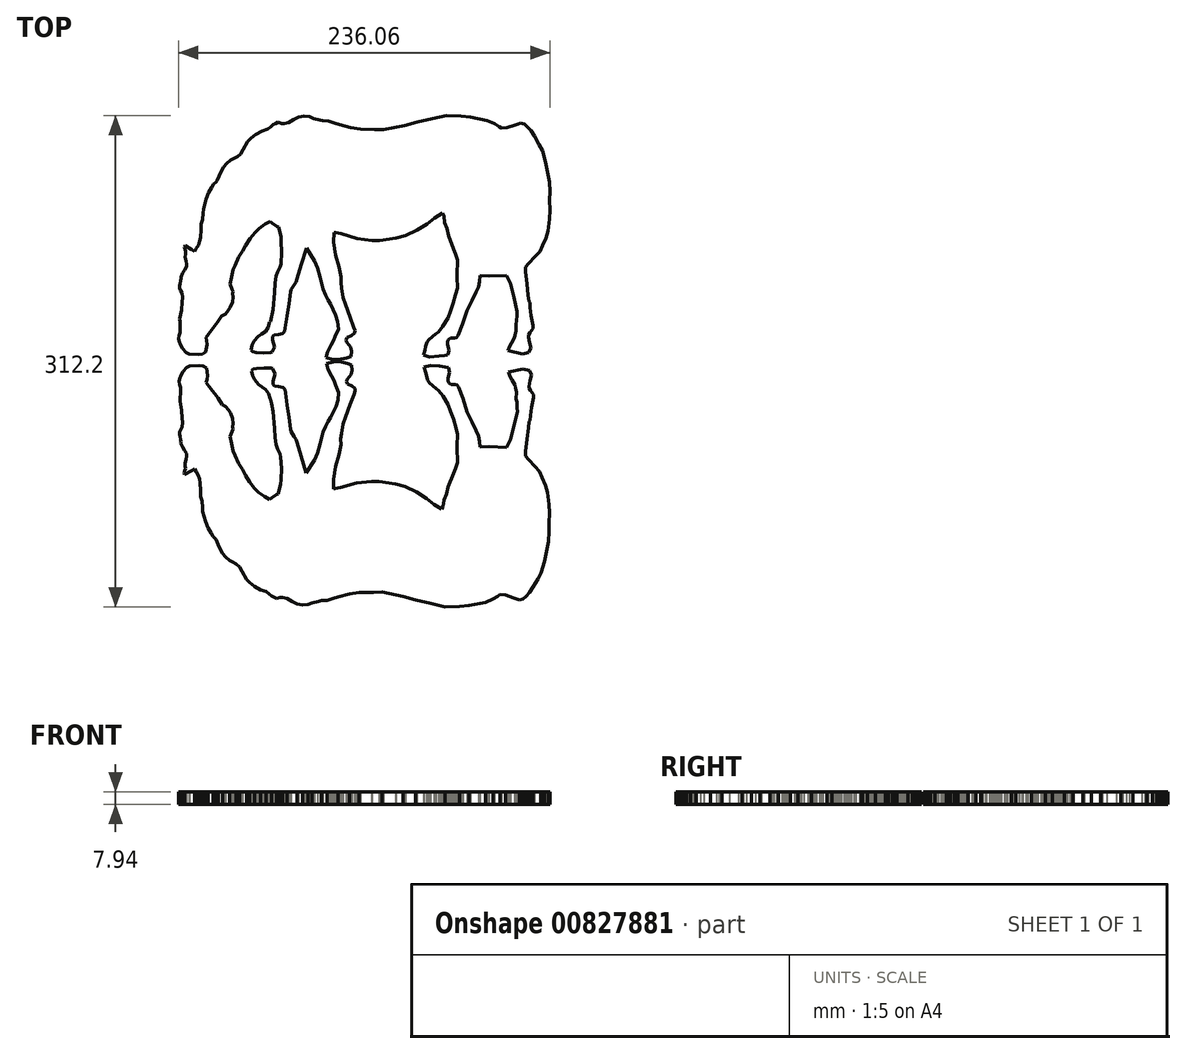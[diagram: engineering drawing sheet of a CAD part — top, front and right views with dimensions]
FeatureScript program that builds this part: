
annotation { "Feature Type Name" : "Feature", "Feature Type Description" : "" }
export const myFeature = defineFeature(function(context is Context, id is Id, definition is map)
    precondition{}
    {
        {
            var Q0;
            Q0=qCreatedBy(makeId("Top.planeOp"),FACE);
            var sketch = newSketch(context, id + "F0", { "sketchPlane" : qUnion([Q0])});
            skLineSegment(sketch, "E0", {"start": v(-100.7, 5.73) * mm, "end": v(-102.84, 4.52) * mm});
            skLineSegment(sketch, "E1", {"start": v(-102.84, 4.52) * mm, "end": v(-105.3, 4.23) * mm});
            skLineSegment(sketch, "E2", {"start": v(-105.3, 4.23) * mm, "end": v(-111.22, 4.55) * mm});
            skLineSegment(sketch, "E3", {"start": v(-111.22, 4.55) * mm, "end": v(-113.36, 5.41) * mm});
            skLineSegment(sketch, "E4", {"start": v(-113.36, 5.41) * mm, "end": v(-115.5, 7.9) * mm});
            skLineSegment(sketch, "E5", {"start": v(-115.5, 7.9) * mm, "end": v(-116.75, 10.19) * mm});
            skLineSegment(sketch, "E6", {"start": v(-116.75, 10.19) * mm, "end": v(-117.54, 12.83) * mm});
            skLineSegment(sketch, "E7", {"start": v(-117.54, 12.83) * mm, "end": v(-118.03, 14.5) * mm});
            skLineSegment(sketch, "E8", {"start": v(-118.03, 14.5) * mm, "end": v(-117.54, 16.28) * mm});
            skLineSegment(sketch, "E9", {"start": v(-117.54, 16.28) * mm, "end": v(-116.98, 18.27) * mm});
            skLineSegment(sketch, "E10", {"start": v(-116.98, 18.27) * mm, "end": v(-117.07, 21.4) * mm});
            skLineSegment(sketch, "E11", {"start": v(-117.07, 21.4) * mm, "end": v(-117.18, 25.1) * mm});
            skLineSegment(sketch, "E12", {"start": v(-117.18, 25.1) * mm, "end": v(-117.22, 26.75) * mm});
            skLineSegment(sketch, "E13", {"start": v(-117.22, 26.75) * mm, "end": v(-116.18, 32.64) * mm});
            skLineSegment(sketch, "E14", {"start": v(-116.18, 32.64) * mm, "end": v(-115.72, 37.46) * mm});
            skLineSegment(sketch, "E15", {"start": v(-115.72, 37.46) * mm, "end": v(-115.44, 40.37) * mm});
            skLineSegment(sketch, "E16", {"start": v(-115.44, 40.37) * mm, "end": v(-115.83, 43.17) * mm});
            skLineSegment(sketch, "E17", {"start": v(-115.83, 43.17) * mm, "end": v(-116.65, 45.02) * mm});
            skLineSegment(sketch, "E18", {"start": v(-116.65, 45.02) * mm, "end": v(-117.3, 46.51) * mm});
            skLineSegment(sketch, "E19", {"start": v(-117.3, 46.51) * mm, "end": v(-117.47, 47.93) * mm});
            skLineSegment(sketch, "E20", {"start": v(-117.47, 47.93) * mm, "end": v(-117.04, 49) * mm});
            skLineSegment(sketch, "E21", {"start": v(-117.04, 49) * mm, "end": v(-116.58, 51.39) * mm});
            skLineSegment(sketch, "E22", {"start": v(-116.58, 51.39) * mm, "end": v(-116.37, 52.44) * mm});
            skLineSegment(sketch, "E23", {"start": v(-116.37, 52.44) * mm, "end": v(-116.54, 53.31) * mm});
            skLineSegment(sketch, "E24", {"start": v(-116.54, 53.31) * mm, "end": v(-115.47, 55.98) * mm});
            skLineSegment(sketch, "E25", {"start": v(-115.47, 55.98) * mm, "end": v(-114.18, 58.03) * mm});
            skLineSegment(sketch, "E26", {"start": v(-114.18, 58.03) * mm, "end": v(-112.93, 60.03) * mm});
            skLineSegment(sketch, "E27", {"start": v(-112.93, 60.03) * mm, "end": v(-112.76, 61.56) * mm});
            skLineSegment(sketch, "E28", {"start": v(-112.76, 61.56) * mm, "end": v(-113.22, 63.77) * mm});
            skLineSegment(sketch, "E29", {"start": v(-113.22, 63.77) * mm, "end": v(-113.73, 66.2) * mm});
            skLineSegment(sketch, "E30", {"start": v(-113.73, 66.2) * mm, "end": v(-113.61, 68.08) * mm});
            skLineSegment(sketch, "E31", {"start": v(-113.61, 68.08) * mm, "end": v(-113.52, 69.6) * mm});
            skLineSegment(sketch, "E32", {"start": v(-113.52, 69.6) * mm, "end": v(-114, 71.1) * mm});
            skLineSegment(sketch, "E33", {"start": v(-114, 71.1) * mm, "end": v(-114.42, 72.38) * mm});
            skLineSegment(sketch, "E34", {"start": v(-114.42, 72.38) * mm, "end": v(-113.93, 73.53) * mm});
            skLineSegment(sketch, "E35", {"start": v(-113.93, 73.53) * mm, "end": v(-109.87, 71.07) * mm});
            skLineSegment(sketch, "E36", {"start": v(-109.87, 71.07) * mm, "end": v(-107.76, 69.8) * mm});
            skLineSegment(sketch, "E37", {"start": v(-107.76, 69.8) * mm, "end": v(-106.77, 71.46) * mm});
            skLineSegment(sketch, "E38", {"start": v(-106.77, 71.46) * mm, "end": v(-105.38, 73.76) * mm});
            skLineSegment(sketch, "E39", {"start": v(-105.38, 73.76) * mm, "end": v(-104.48, 76.16) * mm});
            skLineSegment(sketch, "E40", {"start": v(-104.48, 76.16) * mm, "end": v(-104.05, 78.66) * mm});
            skLineSegment(sketch, "E41", {"start": v(-104.05, 78.66) * mm, "end": v(-103.77, 83.58) * mm});
            skLineSegment(sketch, "E42", {"start": v(-103.77, 83.58) * mm, "end": v(-103.56, 87.1) * mm});
            skLineSegment(sketch, "E43", {"start": v(-103.56, 87.1) * mm, "end": v(-102.6, 90.12) * mm});
            skLineSegment(sketch, "E44", {"start": v(-102.6, 90.12) * mm, "end": v(-102.38, 94.22) * mm});
            skLineSegment(sketch, "E45", {"start": v(-102.38, 94.22) * mm, "end": v(-102.25, 96.66) * mm});
            skLineSegment(sketch, "E46", {"start": v(-102.25, 96.66) * mm, "end": v(-100.48, 103.12) * mm});
            skLineSegment(sketch, "E47", {"start": v(-100.48, 103.12) * mm, "end": v(-98.84, 107.15) * mm});
            skLineSegment(sketch, "E48", {"start": v(-98.84, 107.15) * mm, "end": v(-96.95, 110.4) * mm});
            skLineSegment(sketch, "E49", {"start": v(-96.95, 110.4) * mm, "end": v(-95.64, 112.65) * mm});
            skLineSegment(sketch, "E50", {"start": v(-95.64, 112.65) * mm, "end": v(-94.24, 113.92) * mm});
            skLineSegment(sketch, "E51", {"start": v(-94.24, 113.92) * mm, "end": v(-93.52, 114.58) * mm});
            skLineSegment(sketch, "E52", {"start": v(-93.52, 114.58) * mm, "end": v(-92.42, 117.61) * mm});
            skLineSegment(sketch, "E53", {"start": v(-92.42, 117.61) * mm, "end": v(-90.74, 121.03) * mm});
            skLineSegment(sketch, "E54", {"start": v(-90.74, 121.03) * mm, "end": v(-89.56, 123.44) * mm});
            skLineSegment(sketch, "E55", {"start": v(-89.56, 123.44) * mm, "end": v(-87.46, 125.38) * mm});
            skLineSegment(sketch, "E56", {"start": v(-87.46, 125.38) * mm, "end": v(-84.9, 127.75) * mm});
            skLineSegment(sketch, "E57", {"start": v(-84.9, 127.75) * mm, "end": v(-83.1, 128.71) * mm});
            skLineSegment(sketch, "E58", {"start": v(-83.1, 128.71) * mm, "end": v(-80.64, 130.04) * mm});
            skLineSegment(sketch, "E59", {"start": v(-80.64, 130.04) * mm, "end": v(-78.58, 131.7) * mm});
            skLineSegment(sketch, "E60", {"start": v(-78.58, 131.7) * mm, "end": v(-76.97, 134.56) * mm});
            skLineSegment(sketch, "E61", {"start": v(-76.97, 134.56) * mm, "end": v(-74.14, 139.6) * mm});
            skLineSegment(sketch, "E62", {"start": v(-74.14, 139.6) * mm, "end": v(-72.08, 141.6) * mm});
            skLineSegment(sketch, "E63", {"start": v(-72.08, 141.6) * mm, "end": v(-69.04, 143.96) * mm});
            skLineSegment(sketch, "E64", {"start": v(-69.04, 143.96) * mm, "end": v(-64.94, 146.24) * mm});
            skLineSegment(sketch, "E65", {"start": v(-64.94, 146.24) * mm, "end": v(-61.4, 147.28) * mm});
            skLineSegment(sketch, "E66", {"start": v(-61.4, 147.28) * mm, "end": v(-59.7, 148.7) * mm});
            skLineSegment(sketch, "E67", {"start": v(-59.7, 148.7) * mm, "end": v(-57.97, 150.14) * mm});
            skLineSegment(sketch, "E68", {"start": v(-57.97, 150.14) * mm, "end": v(-56.3, 150.99) * mm});
            skLineSegment(sketch, "E69", {"start": v(-56.3, 150.99) * mm, "end": v(-54.8, 151.75) * mm});
            skLineSegment(sketch, "E70", {"start": v(-54.8, 151.75) * mm, "end": v(-52.55, 151.06) * mm});
            skLineSegment(sketch, "E71", {"start": v(-52.55, 151.06) * mm, "end": v(-50.97, 151.06) * mm});
            skLineSegment(sketch, "E72", {"start": v(-50.97, 151.06) * mm, "end": v(-48.08, 151.7) * mm});
            skLineSegment(sketch, "E73", {"start": v(-48.08, 151.7) * mm, "end": v(-44.9, 153.38) * mm});
            skLineSegment(sketch, "E74", {"start": v(-44.9, 153.38) * mm, "end": v(-41.94, 154.95) * mm});
            skLineSegment(sketch, "E75", {"start": v(-41.94, 154.95) * mm, "end": v(-38.23, 155.6) * mm});
            skLineSegment(sketch, "E76", {"start": v(-38.23, 155.6) * mm, "end": v(-34.95, 155.24) * mm});
            skLineSegment(sketch, "E77", {"start": v(-34.95, 155.24) * mm, "end": v(-32.17, 154.17) * mm});
            skLineSegment(sketch, "E78", {"start": v(-32.17, 154.17) * mm, "end": v(-28.2, 153.2) * mm});
            skLineSegment(sketch, "E79", {"start": v(-28.2, 153.2) * mm, "end": v(-26.4, 152.77) * mm});
            skLineSegment(sketch, "E80", {"start": v(-26.4, 152.77) * mm, "end": v(-22.67, 152.56) * mm});
            skLineSegment(sketch, "E81", {"start": v(-22.67, 152.56) * mm, "end": v(-19, 151.31) * mm});
            skLineSegment(sketch, "E82", {"start": v(-19, 151.31) * mm, "end": v(-15.75, 150.21) * mm});
            skLineSegment(sketch, "E83", {"start": v(-15.75, 150.21) * mm, "end": v(-8.64, 148.28) * mm});
            skLineSegment(sketch, "E84", {"start": v(-8.64, 148.28) * mm, "end": v(-2.42, 147.5) * mm});
            skLineSegment(sketch, "E85", {"start": v(-2.42, 147.5) * mm, "end": v(6.6, 147.18) * mm});
            skLineSegment(sketch, "E86", {"start": v(6.6, 147.18) * mm, "end": v(12.16, 146.98) * mm});
            skLineSegment(sketch, "E87", {"start": v(12.16, 146.98) * mm, "end": v(25.56, 149.6) * mm});
            skLineSegment(sketch, "E88", {"start": v(25.56, 149.6) * mm, "end": v(33.52, 151.92) * mm});
            skLineSegment(sketch, "E89", {"start": v(33.52, 151.92) * mm, "end": v(43.16, 154.07) * mm});
            skLineSegment(sketch, "E90", {"start": v(43.16, 154.07) * mm, "end": v(52.32, 156.1) * mm});
            skLineSegment(sketch, "E91", {"start": v(52.32, 156.1) * mm, "end": v(61.44, 155.75) * mm});
            skLineSegment(sketch, "E92", {"start": v(61.44, 155.75) * mm, "end": v(67.36, 155.03) * mm});
            skLineSegment(sketch, "E93", {"start": v(67.36, 155.03) * mm, "end": v(77.8, 152.96) * mm});
            skLineSegment(sketch, "E94", {"start": v(77.8, 152.96) * mm, "end": v(82.55, 150.82) * mm});
            skLineSegment(sketch, "E95", {"start": v(82.55, 150.82) * mm, "end": v(85.4, 149.04) * mm});
            skLineSegment(sketch, "E96", {"start": v(85.4, 149.04) * mm, "end": v(87.15, 147.95) * mm});
            skLineSegment(sketch, "E97", {"start": v(87.15, 147.95) * mm, "end": v(90.5, 148.25) * mm});
            skLineSegment(sketch, "E98", {"start": v(90.5, 148.25) * mm, "end": v(95.74, 149.97) * mm});
            skLineSegment(sketch, "E99", {"start": v(95.74, 149.97) * mm, "end": v(97.57, 150.56) * mm});
            skLineSegment(sketch, "E100", {"start": v(97.57, 150.56) * mm, "end": v(99.3, 151.12) * mm});
            skLineSegment(sketch, "E101", {"start": v(99.3, 151.12) * mm, "end": v(101.57, 150.54) * mm});
            skLineSegment(sketch, "E102", {"start": v(101.57, 150.54) * mm, "end": v(103.39, 149.11) * mm});
            skLineSegment(sketch, "E103", {"start": v(103.39, 149.11) * mm, "end": v(105.74, 146.44) * mm});
            skLineSegment(sketch, "E104", {"start": v(105.74, 146.44) * mm, "end": v(108.04, 143.04) * mm});
            skLineSegment(sketch, "E105", {"start": v(108.04, 143.04) * mm, "end": v(110.96, 137.65) * mm});
            skLineSegment(sketch, "E106", {"start": v(110.96, 137.65) * mm, "end": v(113.04, 133.84) * mm});
            skLineSegment(sketch, "E107", {"start": v(113.04, 133.84) * mm, "end": v(115.07, 126.52) * mm});
            skLineSegment(sketch, "E108", {"start": v(115.07, 126.52) * mm, "end": v(116.96, 116.99) * mm});
            skLineSegment(sketch, "E109", {"start": v(116.96, 116.99) * mm, "end": v(117.6, 113.8) * mm});
            skLineSegment(sketch, "E110", {"start": v(117.6, 113.8) * mm, "end": v(117.92, 107.7) * mm});
            skLineSegment(sketch, "E111", {"start": v(117.92, 107.7) * mm, "end": v(117.74, 102.32) * mm});
            skLineSegment(sketch, "E112", {"start": v(117.74, 102.32) * mm, "end": v(118.03, 95.84) * mm});
            skLineSegment(sketch, "E113", {"start": v(118.03, 95.84) * mm, "end": v(117.57, 90.43) * mm});
            skLineSegment(sketch, "E114", {"start": v(117.57, 90.43) * mm, "end": v(116.62, 82.82) * mm});
            skLineSegment(sketch, "E115", {"start": v(116.62, 82.82) * mm, "end": v(115.27, 78.29) * mm});
            skLineSegment(sketch, "E116", {"start": v(115.27, 78.29) * mm, "end": v(113.11, 73.3) * mm});
            skLineSegment(sketch, "E117", {"start": v(113.11, 73.3) * mm, "end": v(111.47, 69.5) * mm});
            skLineSegment(sketch, "E118", {"start": v(111.47, 69.5) * mm, "end": v(108.52, 66.36) * mm});
            skLineSegment(sketch, "E119", {"start": v(108.52, 66.36) * mm, "end": v(104.39, 61.97) * mm});
            skLineSegment(sketch, "E120", {"start": v(104.39, 61.97) * mm, "end": v(102.38, 59.83) * mm});
            skLineSegment(sketch, "E121", {"start": v(102.38, 59.83) * mm, "end": v(102.47, 56.84) * mm});
            skLineSegment(sketch, "E122", {"start": v(102.47, 56.84) * mm, "end": v(103.32, 49.1) * mm});
            skLineSegment(sketch, "E123", {"start": v(103.32, 49.1) * mm, "end": v(104.1, 41.96) * mm});
            skLineSegment(sketch, "E124", {"start": v(104.1, 41.96) * mm, "end": v(104.55, 37.87) * mm});
            skLineSegment(sketch, "E125", {"start": v(104.55, 37.87) * mm, "end": v(105.16, 37.35) * mm});
            skLineSegment(sketch, "E126", {"start": v(105.16, 37.35) * mm, "end": v(105.3, 34.17) * mm});
            skLineSegment(sketch, "E127", {"start": v(105.3, 34.17) * mm, "end": v(105.94, 29.06) * mm});
            skLineSegment(sketch, "E128", {"start": v(105.94, 29.06) * mm, "end": v(107.21, 22.74) * mm});
            skLineSegment(sketch, "E129", {"start": v(107.21, 22.74) * mm, "end": v(107.18, 20.76) * mm});
            skLineSegment(sketch, "E130", {"start": v(107.18, 20.76) * mm, "end": v(105.12, 18.24) * mm});
            skLineSegment(sketch, "E131", {"start": v(105.12, 18.24) * mm, "end": v(104.31, 16.61) * mm});
            skLineSegment(sketch, "E132", {"start": v(104.31, 16.61) * mm, "end": v(104.16, 15.47) * mm});
            skLineSegment(sketch, "E133", {"start": v(104.16, 15.47) * mm, "end": v(105.05, 11.8) * mm});
            skLineSegment(sketch, "E134", {"start": v(105.05, 11.8) * mm, "end": v(105.9, 8.25) * mm});
            skLineSegment(sketch, "E135", {"start": v(105.9, 8.25) * mm, "end": v(104.41, 5.47) * mm});
            skLineSegment(sketch, "E136", {"start": v(104.41, 5.47) * mm, "end": v(100.31, 4.62) * mm});
            skLineSegment(sketch, "E137", {"start": v(100.31, 4.62) * mm, "end": v(91.37, 6.67) * mm});
            skLineSegment(sketch, "E138", {"start": v(91.37, 6.67) * mm, "end": v(92.22, 9.32) * mm});
            skLineSegment(sketch, "E139", {"start": v(92.22, 9.32) * mm, "end": v(93.42, 11.44) * mm});
            skLineSegment(sketch, "E140", {"start": v(93.42, 11.44) * mm, "end": v(95.37, 14.89) * mm});
            skLineSegment(sketch, "E141", {"start": v(95.37, 14.89) * mm, "end": v(95.75, 16.5) * mm});
            skLineSegment(sketch, "E142", {"start": v(95.75, 16.5) * mm, "end": v(96.39, 19.19) * mm});
            skLineSegment(sketch, "E143", {"start": v(96.39, 19.19) * mm, "end": v(96.21, 23.65) * mm});
            skLineSegment(sketch, "E144", {"start": v(96.21, 23.65) * mm, "end": v(96.74, 25.59) * mm});
            skLineSegment(sketch, "E145", {"start": v(96.74, 25.59) * mm, "end": v(96.92, 29.2) * mm});
            skLineSegment(sketch, "E146", {"start": v(96.92, 29.2) * mm, "end": v(97.04, 31.61) * mm});
            skLineSegment(sketch, "E147", {"start": v(97.04, 31.61) * mm, "end": v(94.94, 40.44) * mm});
            skLineSegment(sketch, "E148", {"start": v(94.94, 40.44) * mm, "end": v(92.83, 49.31) * mm});
            skLineSegment(sketch, "E149", {"start": v(92.83, 49.31) * mm, "end": v(90.27, 54.43) * mm});
            skLineSegment(sketch, "E150", {"start": v(90.27, 54.43) * mm, "end": v(79.12, 54.07) * mm});
            skLineSegment(sketch, "E151", {"start": v(79.12, 54.07) * mm, "end": v(73.57, 54.32) * mm});
            skLineSegment(sketch, "E152", {"start": v(73.57, 54.32) * mm, "end": v(73.11, 50.75) * mm});
            skLineSegment(sketch, "E153", {"start": v(73.11, 50.75) * mm, "end": v(72.66, 47.22) * mm});
            skLineSegment(sketch, "E154", {"start": v(72.66, 47.22) * mm, "end": v(70.99, 43.89) * mm});
            skLineSegment(sketch, "E155", {"start": v(70.99, 43.89) * mm, "end": v(68.3, 38.52) * mm});
            skLineSegment(sketch, "E156", {"start": v(68.3, 38.52) * mm, "end": v(65.06, 32.05) * mm});
            skLineSegment(sketch, "E157", {"start": v(65.06, 32.05) * mm, "end": v(62.46, 23.55) * mm});
            skLineSegment(sketch, "E158", {"start": v(62.46, 23.55) * mm, "end": v(59.6, 16.19) * mm});
            skLineSegment(sketch, "E159", {"start": v(59.6, 16.19) * mm, "end": v(58.43, 15.02) * mm});
            skLineSegment(sketch, "E160", {"start": v(58.43, 15.02) * mm, "end": v(57.36, 14.7) * mm});
            skLineSegment(sketch, "E161", {"start": v(57.36, 14.7) * mm, "end": v(54.85, 14.62) * mm});
            skLineSegment(sketch, "E162", {"start": v(54.85, 14.62) * mm, "end": v(53.44, 13.7) * mm});
            skLineSegment(sketch, "E163", {"start": v(53.44, 13.7) * mm, "end": v(52.73, 12.6) * mm});
            skLineSegment(sketch, "E164", {"start": v(52.73, 12.6) * mm, "end": v(52.88, 10.56) * mm});
            skLineSegment(sketch, "E165", {"start": v(52.88, 10.56) * mm, "end": v(53.9, 7.03) * mm});
            skLineSegment(sketch, "E166", {"start": v(53.9, 7.03) * mm, "end": v(53.48, 5.65) * mm});
            skLineSegment(sketch, "E167", {"start": v(53.48, 5.65) * mm, "end": v(52.94, 3.9) * mm});
            skLineSegment(sketch, "E168", {"start": v(52.94, 3.9) * mm, "end": v(50.88, 3.62) * mm});
            skLineSegment(sketch, "E169", {"start": v(50.88, 3.62) * mm, "end": v(47.5, 3.16) * mm});
            skLineSegment(sketch, "E170", {"start": v(47.5, 3.16) * mm, "end": v(41.55, 2.8) * mm});
            skLineSegment(sketch, "E171", {"start": v(41.55, 2.8) * mm, "end": v(37.66, 3.83) * mm});
            skLineSegment(sketch, "E172", {"start": v(37.66, 3.83) * mm, "end": v(38.44, 6.97) * mm});
            skLineSegment(sketch, "E173", {"start": v(38.44, 6.97) * mm, "end": v(39.02, 9.32) * mm});
            skLineSegment(sketch, "E174", {"start": v(39.02, 9.32) * mm, "end": v(39.7, 12.1) * mm});
            skLineSegment(sketch, "E175", {"start": v(39.7, 12.1) * mm, "end": v(41.21, 13.92) * mm});
            skLineSegment(sketch, "E176", {"start": v(41.21, 13.92) * mm, "end": v(45.14, 17.42) * mm});
            skLineSegment(sketch, "E177", {"start": v(45.14, 17.42) * mm, "end": v(47.01, 18.55) * mm});
            skLineSegment(sketch, "E178", {"start": v(47.01, 18.55) * mm, "end": v(49.7, 22.04) * mm});
            skLineSegment(sketch, "E179", {"start": v(49.7, 22.04) * mm, "end": v(53, 27.39) * mm});
            skLineSegment(sketch, "E180", {"start": v(53, 27.39) * mm, "end": v(54.73, 32.02) * mm});
            skLineSegment(sketch, "E181", {"start": v(54.73, 32.02) * mm, "end": v(56.45, 36.61) * mm});
            skLineSegment(sketch, "E182", {"start": v(56.45, 36.61) * mm, "end": v(58.05, 42.43) * mm});
            skLineSegment(sketch, "E183", {"start": v(58.05, 42.43) * mm, "end": v(59.2, 46.55) * mm});
            skLineSegment(sketch, "E184", {"start": v(59.2, 46.55) * mm, "end": v(58.8, 53.5) * mm});
            skLineSegment(sketch, "E185", {"start": v(58.8, 53.5) * mm, "end": v(59.01, 57.89) * mm});
            skLineSegment(sketch, "E186", {"start": v(59.01, 57.89) * mm, "end": v(59.17, 61.19) * mm});
            skLineSegment(sketch, "E187", {"start": v(59.17, 61.19) * mm, "end": v(59.32, 64.21) * mm});
            skLineSegment(sketch, "E188", {"start": v(59.32, 64.21) * mm, "end": v(57.95, 67.97) * mm});
            skLineSegment(sketch, "E189", {"start": v(57.95, 67.97) * mm, "end": v(56.76, 71.24) * mm});
            skLineSegment(sketch, "E190", {"start": v(56.76, 71.24) * mm, "end": v(53.52, 79.78) * mm});
            skLineSegment(sketch, "E191", {"start": v(53.52, 79.78) * mm, "end": v(52.4, 84.29) * mm});
            skLineSegment(sketch, "E192", {"start": v(52.4, 84.29) * mm, "end": v(50.9, 88.06) * mm});
            skLineSegment(sketch, "E193", {"start": v(50.9, 88.06) * mm, "end": v(50.5, 92.27) * mm});
            skLineSegment(sketch, "E194", {"start": v(50.5, 92.27) * mm, "end": v(49.52, 93.95) * mm});
            skLineSegment(sketch, "E195", {"start": v(49.52, 93.95) * mm, "end": v(44.7, 91.07) * mm});
            skLineSegment(sketch, "E196", {"start": v(44.7, 91.07) * mm, "end": v(39.75, 87.18) * mm});
            skLineSegment(sketch, "E197", {"start": v(39.75, 87.18) * mm, "end": v(33.54, 83.37) * mm});
            skLineSegment(sketch, "E198", {"start": v(33.54, 83.37) * mm, "end": v(26.01, 79.84) * mm});
            skLineSegment(sketch, "E199", {"start": v(26.01, 79.84) * mm, "end": v(20.1, 78.2) * mm});
            skLineSegment(sketch, "E200", {"start": v(20.1, 78.2) * mm, "end": v(9.61, 76.74) * mm});
            skLineSegment(sketch, "E201", {"start": v(9.61, 76.74) * mm, "end": v(4.97, 76.77) * mm});
            skLineSegment(sketch, "E202", {"start": v(4.97, 76.77) * mm, "end": v(-4.73, 77.97) * mm});
            skLineSegment(sketch, "E203", {"start": v(-4.73, 77.97) * mm, "end": v(-14.7, 80.93) * mm});
            skLineSegment(sketch, "E204", {"start": v(-14.7, 80.93) * mm, "end": v(-18.43, 81.56) * mm});
            skLineSegment(sketch, "E205", {"start": v(-18.43, 81.56) * mm, "end": v(-19.37, 81.72) * mm});
            skLineSegment(sketch, "E206", {"start": v(-19.37, 81.72) * mm, "end": v(-19.44, 75.66) * mm});
            skLineSegment(sketch, "E207", {"start": v(-19.44, 75.66) * mm, "end": v(-18.17, 67.45) * mm});
            skLineSegment(sketch, "E208", {"start": v(-18.17, 67.45) * mm, "end": v(-15.96, 59.93) * mm});
            skLineSegment(sketch, "E209", {"start": v(-15.96, 59.93) * mm, "end": v(-15.14, 55.01) * mm});
            skLineSegment(sketch, "E210", {"start": v(-15.14, 55.01) * mm, "end": v(-14.88, 53.5) * mm});
            skLineSegment(sketch, "E211", {"start": v(-14.88, 53.5) * mm, "end": v(-14.95, 50.03) * mm});
            skLineSegment(sketch, "E212", {"start": v(-14.95, 50.03) * mm, "end": v(-14.61, 46.44) * mm});
            skLineSegment(sketch, "E213", {"start": v(-14.61, 46.44) * mm, "end": v(-13.5, 40.34) * mm});
            skLineSegment(sketch, "E214", {"start": v(-13.5, 40.34) * mm, "end": v(-11.96, 36.08) * mm});
            skLineSegment(sketch, "E215", {"start": v(-11.96, 36.08) * mm, "end": v(-9.1, 28.1) * mm});
            skLineSegment(sketch, "E216", {"start": v(-9.1, 28.1) * mm, "end": v(-6.74, 21.56) * mm});
            skLineSegment(sketch, "E217", {"start": v(-6.74, 21.56) * mm, "end": v(-6.01, 19.55) * mm});
            skLineSegment(sketch, "E218", {"start": v(-6.01, 19.55) * mm, "end": v(-6.2, 17.79) * mm});
            skLineSegment(sketch, "E219", {"start": v(-6.2, 17.79) * mm, "end": v(-8.22, 16.37) * mm});
            skLineSegment(sketch, "E220", {"start": v(-8.22, 16.37) * mm, "end": v(-10.9, 14.98) * mm});
            skLineSegment(sketch, "E221", {"start": v(-10.9, 14.98) * mm, "end": v(-11.47, 13.53) * mm});
            skLineSegment(sketch, "E222", {"start": v(-11.47, 13.53) * mm, "end": v(-11.17, 12.03) * mm});
            skLineSegment(sketch, "E223", {"start": v(-11.17, 12.03) * mm, "end": v(-9.86, 10.35) * mm});
            skLineSegment(sketch, "E224", {"start": v(-9.86, 10.35) * mm, "end": v(-8.7, 8.85) * mm});
            skLineSegment(sketch, "E225", {"start": v(-8.7, 8.85) * mm, "end": v(-8.18, 6.38) * mm});
            skLineSegment(sketch, "E226", {"start": v(-8.18, 6.38) * mm, "end": v(-8.44, 2.89) * mm});
            skLineSegment(sketch, "E227", {"start": v(-8.44, 2.89) * mm, "end": v(-11.17, 1.92) * mm});
            skLineSegment(sketch, "E228", {"start": v(-11.17, 1.92) * mm, "end": v(-16.3, 0.94) * mm});
            skLineSegment(sketch, "E229", {"start": v(-16.3, 0.94) * mm, "end": v(-20.12, 1.05) * mm});
            skLineSegment(sketch, "E230", {"start": v(-20.12, 1.05) * mm, "end": v(-24.27, 2.25) * mm});
            skLineSegment(sketch, "E231", {"start": v(-24.27, 2.25) * mm, "end": v(-23.52, 5.99) * mm});
            skLineSegment(sketch, "E232", {"start": v(-23.52, 5.99) * mm, "end": v(-21.2, 10.18) * mm});
            skLineSegment(sketch, "E233", {"start": v(-21.2, 10.18) * mm, "end": v(-19.65, 12.98) * mm});
            skLineSegment(sketch, "E234", {"start": v(-19.65, 12.98) * mm, "end": v(-18.62, 15.82) * mm});
            skLineSegment(sketch, "E235", {"start": v(-18.62, 15.82) * mm, "end": v(-16.49, 20.51) * mm});
            skLineSegment(sketch, "E236", {"start": v(-16.49, 20.51) * mm, "end": v(-16.86, 25.08) * mm});
            skLineSegment(sketch, "E237", {"start": v(-16.86, 25.08) * mm, "end": v(-18.29, 29.23) * mm});
            skLineSegment(sketch, "E238", {"start": v(-18.29, 29.23) * mm, "end": v(-21.5, 36.46) * mm});
            skLineSegment(sketch, "E239", {"start": v(-21.5, 36.46) * mm, "end": v(-23, 38.82) * mm});
            skLineSegment(sketch, "E240", {"start": v(-23, 38.82) * mm, "end": v(-24.58, 42.08) * mm});
            skLineSegment(sketch, "E241", {"start": v(-24.58, 42.08) * mm, "end": v(-26.32, 45.7) * mm});
            skLineSegment(sketch, "E242", {"start": v(-26.32, 45.7) * mm, "end": v(-28.02, 53.4) * mm});
            skLineSegment(sketch, "E243", {"start": v(-28.02, 53.4) * mm, "end": v(-29.74, 59.08) * mm});
            skLineSegment(sketch, "E244", {"start": v(-29.74, 59.08) * mm, "end": v(-31.62, 63.58) * mm});
            skLineSegment(sketch, "E245", {"start": v(-31.62, 63.58) * mm, "end": v(-36.7, 71.73) * mm});
            skLineSegment(sketch, "E246", {"start": v(-36.7, 71.73) * mm, "end": v(-40.05, 61.07) * mm});
            skLineSegment(sketch, "E247", {"start": v(-40.05, 61.07) * mm, "end": v(-42.77, 52.38) * mm});
            skLineSegment(sketch, "E248", {"start": v(-42.77, 52.38) * mm, "end": v(-43.4, 50.4) * mm});
            skLineSegment(sketch, "E249", {"start": v(-43.4, 50.4) * mm, "end": v(-44.58, 48.5) * mm});
            skLineSegment(sketch, "E250", {"start": v(-44.58, 48.5) * mm, "end": v(-46.43, 45.54) * mm});
            skLineSegment(sketch, "E251", {"start": v(-46.43, 45.54) * mm, "end": v(-46.82, 43.85) * mm});
            skLineSegment(sketch, "E252", {"start": v(-46.82, 43.85) * mm, "end": v(-47.94, 36.52) * mm});
            skLineSegment(sketch, "E253", {"start": v(-47.94, 36.52) * mm, "end": v(-49.14, 28.74) * mm});
            skLineSegment(sketch, "E254", {"start": v(-49.14, 28.74) * mm, "end": v(-50.32, 21) * mm});
            skLineSegment(sketch, "E255", {"start": v(-50.32, 21) * mm, "end": v(-50.64, 18.9) * mm});
            skLineSegment(sketch, "E256", {"start": v(-50.64, 18.9) * mm, "end": v(-51.8, 17.61) * mm});
            skLineSegment(sketch, "E257", {"start": v(-51.8, 17.61) * mm, "end": v(-54.64, 16.86) * mm});
            skLineSegment(sketch, "E258", {"start": v(-54.64, 16.86) * mm, "end": v(-57.23, 16.6) * mm});
            skLineSegment(sketch, "E259", {"start": v(-57.23, 16.6) * mm, "end": v(-58.2, 15.74) * mm});
            skLineSegment(sketch, "E260", {"start": v(-58.2, 15.74) * mm, "end": v(-58.36, 13.53) * mm});
            skLineSegment(sketch, "E261", {"start": v(-58.36, 13.53) * mm, "end": v(-56.93, 8.96) * mm});
            skLineSegment(sketch, "E262", {"start": v(-56.93, 8.96) * mm, "end": v(-58.66, 5.7) * mm});
            skLineSegment(sketch, "E263", {"start": v(-58.66, 5.7) * mm, "end": v(-59.48, 5.4) * mm});
            skLineSegment(sketch, "E264", {"start": v(-59.48, 5.4) * mm, "end": v(-64.1, 5.25) * mm});
            skLineSegment(sketch, "E265", {"start": v(-64.1, 5.25) * mm, "end": v(-68.93, 5.55) * mm});
            skLineSegment(sketch, "E266", {"start": v(-68.93, 5.55) * mm, "end": v(-70.91, 6.14) * mm});
            skLineSegment(sketch, "E267", {"start": v(-70.91, 6.14) * mm, "end": v(-72.03, 7.2) * mm});
            skLineSegment(sketch, "E268", {"start": v(-72.03, 7.2) * mm, "end": v(-71.44, 10.22) * mm});
            skLineSegment(sketch, "E269", {"start": v(-71.44, 10.22) * mm, "end": v(-70.01, 12.69) * mm});
            skLineSegment(sketch, "E270", {"start": v(-70.01, 12.69) * mm, "end": v(-67.55, 15.83) * mm});
            skLineSegment(sketch, "E271", {"start": v(-67.55, 15.83) * mm, "end": v(-65.15, 17.36) * mm});
            skLineSegment(sketch, "E272", {"start": v(-65.15, 17.36) * mm, "end": v(-62.88, 18.81) * mm});
            skLineSegment(sketch, "E273", {"start": v(-62.88, 18.81) * mm, "end": v(-61.11, 21.44) * mm});
            skLineSegment(sketch, "E274", {"start": v(-61.11, 21.44) * mm, "end": v(-60.25, 24.75) * mm});
            skLineSegment(sketch, "E275", {"start": v(-60.25, 24.75) * mm, "end": v(-59.68, 25.23) * mm});
            skLineSegment(sketch, "E276", {"start": v(-59.68, 25.23) * mm, "end": v(-59.16, 27.7) * mm});
            skLineSegment(sketch, "E277", {"start": v(-59.16, 27.7) * mm, "end": v(-58.05, 32.92) * mm});
            skLineSegment(sketch, "E278", {"start": v(-58.05, 32.92) * mm, "end": v(-57.06, 43.76) * mm});
            skLineSegment(sketch, "E279", {"start": v(-57.06, 43.76) * mm, "end": v(-56.54, 49.5) * mm});
            skLineSegment(sketch, "E280", {"start": v(-56.54, 49.5) * mm, "end": v(-55.98, 53.99) * mm});
            skLineSegment(sketch, "E281", {"start": v(-55.98, 53.99) * mm, "end": v(-55.12, 56.53) * mm});
            skLineSegment(sketch, "E282", {"start": v(-55.12, 56.53) * mm, "end": v(-53.55, 59.75) * mm});
            skLineSegment(sketch, "E283", {"start": v(-53.55, 59.75) * mm, "end": v(-53.02, 61.78) * mm});
            skLineSegment(sketch, "E284", {"start": v(-53.02, 61.78) * mm, "end": v(-52.53, 69.2) * mm});
            skLineSegment(sketch, "E285", {"start": v(-52.53, 69.2) * mm, "end": v(-52.8, 75.94) * mm});
            skLineSegment(sketch, "E286", {"start": v(-52.8, 75.94) * mm, "end": v(-52.93, 79.31) * mm});
            skLineSegment(sketch, "E287", {"start": v(-52.93, 79.31) * mm, "end": v(-54.37, 85.18) * mm});
            skLineSegment(sketch, "E288", {"start": v(-54.37, 85.18) * mm, "end": v(-55.57, 85.6) * mm});
            skLineSegment(sketch, "E289", {"start": v(-55.57, 85.6) * mm, "end": v(-58.48, 87.76) * mm});
            skLineSegment(sketch, "E290", {"start": v(-58.48, 87.76) * mm, "end": v(-59.78, 88.72) * mm});
            skLineSegment(sketch, "E291", {"start": v(-59.78, 88.72) * mm, "end": v(-63.05, 86.98) * mm});
            skLineSegment(sketch, "E292", {"start": v(-63.05, 86.98) * mm, "end": v(-66.79, 84.36) * mm});
            skLineSegment(sketch, "E293", {"start": v(-66.79, 84.36) * mm, "end": v(-69.45, 81.81) * mm});
            skLineSegment(sketch, "E294", {"start": v(-69.45, 81.81) * mm, "end": v(-72.55, 77.89) * mm});
            skLineSegment(sketch, "E295", {"start": v(-72.55, 77.89) * mm, "end": v(-75.32, 73.59) * mm});
            skLineSegment(sketch, "E296", {"start": v(-75.32, 73.59) * mm, "end": v(-77.26, 69.81) * mm});
            skLineSegment(sketch, "E297", {"start": v(-77.26, 69.81) * mm, "end": v(-79.74, 66.06) * mm});
            skLineSegment(sketch, "E298", {"start": v(-79.74, 66.06) * mm, "end": v(-82.13, 60.9) * mm});
            skLineSegment(sketch, "E299", {"start": v(-82.13, 60.9) * mm, "end": v(-83.38, 58.21) * mm});
            skLineSegment(sketch, "E300", {"start": v(-83.38, 58.21) * mm, "end": v(-84.34, 53.37) * mm});
            skLineSegment(sketch, "E301", {"start": v(-84.34, 53.37) * mm, "end": v(-85.23, 48.93) * mm});
            skLineSegment(sketch, "E302", {"start": v(-85.23, 48.93) * mm, "end": v(-84, 45.66) * mm});
            skLineSegment(sketch, "E303", {"start": v(-84, 45.66) * mm, "end": v(-83.5, 44.29) * mm});
            skLineSegment(sketch, "E304", {"start": v(-83.5, 44.29) * mm, "end": v(-83.78, 43) * mm});
            skLineSegment(sketch, "E305", {"start": v(-83.78, 43) * mm, "end": v(-83.48, 40.86) * mm});
            skLineSegment(sketch, "E306", {"start": v(-83.48, 40.86) * mm, "end": v(-83.86, 37.64) * mm});
            skLineSegment(sketch, "E307", {"start": v(-83.86, 37.64) * mm, "end": v(-85.2, 34.09) * mm});
            skLineSegment(sketch, "E308", {"start": v(-85.2, 34.09) * mm, "end": v(-86.52, 32.25) * mm});
            skLineSegment(sketch, "E309", {"start": v(-86.52, 32.25) * mm, "end": v(-88.23, 29.85) * mm});
            skLineSegment(sketch, "E310", {"start": v(-88.23, 29.85) * mm, "end": v(-90.63, 28.66) * mm});
            skLineSegment(sketch, "E311", {"start": v(-90.63, 28.66) * mm, "end": v(-93.14, 24.76) * mm});
            skLineSegment(sketch, "E312", {"start": v(-93.14, 24.76) * mm, "end": v(-98.8, 17.34) * mm});
            skLineSegment(sketch, "E313", {"start": v(-98.8, 17.34) * mm, "end": v(-100.66, 14.9) * mm});
            skLineSegment(sketch, "E314", {"start": v(-100.66, 14.9) * mm, "end": v(-100.07, 13.04) * mm});
            skLineSegment(sketch, "E315", {"start": v(-100.07, 13.04) * mm, "end": v(-99.85, 10.45) * mm});
            skLineSegment(sketch, "E316", {"start": v(-99.85, 10.45) * mm, "end": v(-100.7, 5.73) * mm});
            skLineSegment(sketch, "E317", {"start": v(-100.33, -4.42) * mm, "end": v(-102.46, -3.2) * mm});
            skLineSegment(sketch, "E318", {"start": v(-102.46, -3.2) * mm, "end": v(-104.92, -2.89) * mm});
            skLineSegment(sketch, "E319", {"start": v(-104.92, -2.89) * mm, "end": v(-110.84, -3.16) * mm});
            skLineSegment(sketch, "E320", {"start": v(-110.84, -3.16) * mm, "end": v(-113, -4) * mm});
            skLineSegment(sketch, "E321", {"start": v(-113, -4) * mm, "end": v(-115.15, -6.47) * mm});
            skLineSegment(sketch, "E322", {"start": v(-115.15, -6.47) * mm, "end": v(-116.42, -8.74) * mm});
            skLineSegment(sketch, "E323", {"start": v(-116.42, -8.74) * mm, "end": v(-117.23, -11.37) * mm});
            skLineSegment(sketch, "E324", {"start": v(-117.23, -11.37) * mm, "end": v(-117.74, -13.04) * mm});
            skLineSegment(sketch, "E325", {"start": v(-117.74, -13.04) * mm, "end": v(-117.26, -14.83) * mm});
            skLineSegment(sketch, "E326", {"start": v(-117.26, -14.83) * mm, "end": v(-116.72, -16.83) * mm});
            skLineSegment(sketch, "E327", {"start": v(-116.72, -16.83) * mm, "end": v(-116.84, -19.95) * mm});
            skLineSegment(sketch, "E328", {"start": v(-116.84, -19.95) * mm, "end": v(-116.97, -23.65) * mm});
            skLineSegment(sketch, "E329", {"start": v(-116.97, -23.65) * mm, "end": v(-117.03, -25.3) * mm});
            skLineSegment(sketch, "E330", {"start": v(-117.03, -25.3) * mm, "end": v(-116.04, -31.2) * mm});
            skLineSegment(sketch, "E331", {"start": v(-116.04, -31.2) * mm, "end": v(-115.62, -36.02) * mm});
            skLineSegment(sketch, "E332", {"start": v(-115.62, -36.02) * mm, "end": v(-115.36, -38.94) * mm});
            skLineSegment(sketch, "E333", {"start": v(-115.36, -38.94) * mm, "end": v(-115.78, -41.73) * mm});
            skLineSegment(sketch, "E334", {"start": v(-115.78, -41.73) * mm, "end": v(-116.62, -43.58) * mm});
            skLineSegment(sketch, "E335", {"start": v(-116.62, -43.58) * mm, "end": v(-117.29, -45.06) * mm});
            skLineSegment(sketch, "E336", {"start": v(-117.29, -45.06) * mm, "end": v(-117.46, -46.47) * mm});
            skLineSegment(sketch, "E337", {"start": v(-117.46, -46.47) * mm, "end": v(-117.04, -47.55) * mm});
            skLineSegment(sketch, "E338", {"start": v(-117.04, -47.55) * mm, "end": v(-116.6, -49.94) * mm});
            skLineSegment(sketch, "E339", {"start": v(-116.6, -49.94) * mm, "end": v(-116.4, -51) * mm});
            skLineSegment(sketch, "E340", {"start": v(-116.4, -51) * mm, "end": v(-116.58, -51.87) * mm});
            skLineSegment(sketch, "E341", {"start": v(-116.58, -51.87) * mm, "end": v(-115.53, -54.55) * mm});
            skLineSegment(sketch, "E342", {"start": v(-115.53, -54.55) * mm, "end": v(-114.26, -56.6) * mm});
            skLineSegment(sketch, "E343", {"start": v(-114.26, -56.6) * mm, "end": v(-113.02, -58.62) * mm});
            skLineSegment(sketch, "E344", {"start": v(-113.02, -58.62) * mm, "end": v(-112.87, -60.15) * mm});
            skLineSegment(sketch, "E345", {"start": v(-112.87, -60.15) * mm, "end": v(-113.35, -62.35) * mm});
            skLineSegment(sketch, "E346", {"start": v(-113.35, -62.35) * mm, "end": v(-113.88, -64.78) * mm});
            skLineSegment(sketch, "E347", {"start": v(-113.88, -64.78) * mm, "end": v(-113.78, -66.66) * mm});
            skLineSegment(sketch, "E348", {"start": v(-113.78, -66.66) * mm, "end": v(-113.7, -68.18) * mm});
            skLineSegment(sketch, "E349", {"start": v(-113.7, -68.18) * mm, "end": v(-114.2, -69.68) * mm});
            skLineSegment(sketch, "E350", {"start": v(-114.2, -69.68) * mm, "end": v(-114.62, -70.95) * mm});
            skLineSegment(sketch, "E351", {"start": v(-114.62, -70.95) * mm, "end": v(-114.15, -72.1) * mm});
            skLineSegment(sketch, "E352", {"start": v(-114.15, -72.1) * mm, "end": v(-110.06, -69.68) * mm});
            skLineSegment(sketch, "E353", {"start": v(-110.06, -69.68) * mm, "end": v(-107.94, -68.42) * mm});
            skLineSegment(sketch, "E354", {"start": v(-107.94, -68.42) * mm, "end": v(-106.96, -70.1) * mm});
            skLineSegment(sketch, "E355", {"start": v(-106.96, -70.1) * mm, "end": v(-105.6, -72.41) * mm});
            skLineSegment(sketch, "E356", {"start": v(-105.6, -72.41) * mm, "end": v(-104.72, -74.82) * mm});
            skLineSegment(sketch, "E357", {"start": v(-104.72, -74.82) * mm, "end": v(-104.31, -77.32) * mm});
            skLineSegment(sketch, "E358", {"start": v(-104.31, -77.32) * mm, "end": v(-104.07, -82.24) * mm});
            skLineSegment(sketch, "E359", {"start": v(-104.07, -82.24) * mm, "end": v(-103.9, -85.77) * mm});
            skLineSegment(sketch, "E360", {"start": v(-103.9, -85.77) * mm, "end": v(-102.95, -88.8) * mm});
            skLineSegment(sketch, "E361", {"start": v(-102.95, -88.8) * mm, "end": v(-102.77, -92.9) * mm});
            skLineSegment(sketch, "E362", {"start": v(-102.77, -92.9) * mm, "end": v(-102.66, -95.34) * mm});
            skLineSegment(sketch, "E363", {"start": v(-102.66, -95.34) * mm, "end": v(-100.95, -101.81) * mm});
            skLineSegment(sketch, "E364", {"start": v(-100.95, -101.81) * mm, "end": v(-99.34, -105.86) * mm});
            skLineSegment(sketch, "E365", {"start": v(-99.34, -105.86) * mm, "end": v(-97.48, -109.12) * mm});
            skLineSegment(sketch, "E366", {"start": v(-97.48, -109.12) * mm, "end": v(-96.18, -111.39) * mm});
            skLineSegment(sketch, "E367", {"start": v(-96.18, -111.39) * mm, "end": v(-94.8, -112.67) * mm});
            skLineSegment(sketch, "E368", {"start": v(-94.8, -112.67) * mm, "end": v(-94.08, -113.33) * mm});
            skLineSegment(sketch, "E369", {"start": v(-94.08, -113.33) * mm, "end": v(-93, -116.37) * mm});
            skLineSegment(sketch, "E370", {"start": v(-93, -116.37) * mm, "end": v(-91.36, -119.8) * mm});
            skLineSegment(sketch, "E371", {"start": v(-91.36, -119.8) * mm, "end": v(-90.2, -122.22) * mm});
            skLineSegment(sketch, "E372", {"start": v(-90.2, -122.22) * mm, "end": v(-88.12, -124.19) * mm});
            skLineSegment(sketch, "E373", {"start": v(-88.12, -124.19) * mm, "end": v(-85.58, -126.58) * mm});
            skLineSegment(sketch, "E374", {"start": v(-85.58, -126.58) * mm, "end": v(-83.8, -127.55) * mm});
            skLineSegment(sketch, "E375", {"start": v(-83.8, -127.55) * mm, "end": v(-81.34, -128.9) * mm});
            skLineSegment(sketch, "E376", {"start": v(-81.34, -128.9) * mm, "end": v(-79.29, -130.59) * mm});
            skLineSegment(sketch, "E377", {"start": v(-79.29, -130.59) * mm, "end": v(-77.7, -133.45) * mm});
            skLineSegment(sketch, "E378", {"start": v(-77.7, -133.45) * mm, "end": v(-74.92, -138.5) * mm});
            skLineSegment(sketch, "E379", {"start": v(-74.92, -138.5) * mm, "end": v(-72.88, -140.53) * mm});
            skLineSegment(sketch, "E380", {"start": v(-72.88, -140.53) * mm, "end": v(-69.86, -142.92) * mm});
            skLineSegment(sketch, "E381", {"start": v(-69.86, -142.92) * mm, "end": v(-65.77, -145.24) * mm});
            skLineSegment(sketch, "E382", {"start": v(-65.77, -145.24) * mm, "end": v(-62.25, -146.3) * mm});
            skLineSegment(sketch, "E383", {"start": v(-62.25, -146.3) * mm, "end": v(-60.55, -147.74) * mm});
            skLineSegment(sketch, "E384", {"start": v(-60.55, -147.74) * mm, "end": v(-58.84, -149.2) * mm});
            skLineSegment(sketch, "E385", {"start": v(-58.84, -149.2) * mm, "end": v(-57.18, -150.06) * mm});
            skLineSegment(sketch, "E386", {"start": v(-57.18, -150.06) * mm, "end": v(-55.7, -150.83) * mm});
            skLineSegment(sketch, "E387", {"start": v(-55.7, -150.83) * mm, "end": v(-53.43, -150.16) * mm});
            skLineSegment(sketch, "E388", {"start": v(-53.43, -150.16) * mm, "end": v(-51.85, -150.18) * mm});
            skLineSegment(sketch, "E389", {"start": v(-51.85, -150.18) * mm, "end": v(-48.97, -150.84) * mm});
            skLineSegment(sketch, "E390", {"start": v(-48.97, -150.84) * mm, "end": v(-45.8, -152.55) * mm});
            skLineSegment(sketch, "E391", {"start": v(-45.8, -152.55) * mm, "end": v(-42.85, -154.14) * mm});
            skLineSegment(sketch, "E392", {"start": v(-42.85, -154.14) * mm, "end": v(-39.15, -154.82) * mm});
            skLineSegment(sketch, "E393", {"start": v(-39.15, -154.82) * mm, "end": v(-35.87, -154.49) * mm});
            skLineSegment(sketch, "E394", {"start": v(-35.87, -154.49) * mm, "end": v(-33.08, -153.44) * mm});
            skLineSegment(sketch, "E395", {"start": v(-33.08, -153.44) * mm, "end": v(-29.1, -152.51) * mm});
            skLineSegment(sketch, "E396", {"start": v(-29.1, -152.51) * mm, "end": v(-27.3, -152.1) * mm});
            skLineSegment(sketch, "E397", {"start": v(-27.3, -152.1) * mm, "end": v(-23.56, -151.92) * mm});
            skLineSegment(sketch, "E398", {"start": v(-23.56, -151.92) * mm, "end": v(-19.88, -150.7) * mm});
            skLineSegment(sketch, "E399", {"start": v(-19.88, -150.7) * mm, "end": v(-16.62, -149.63) * mm});
            skLineSegment(sketch, "E400", {"start": v(-16.62, -149.63) * mm, "end": v(-9.5, -147.76) * mm});
            skLineSegment(sketch, "E401", {"start": v(-9.5, -147.76) * mm, "end": v(-3.27, -147.03) * mm});
            skLineSegment(sketch, "E402", {"start": v(-3.27, -147.03) * mm, "end": v(5.76, -146.79) * mm});
            skLineSegment(sketch, "E403", {"start": v(5.76, -146.79) * mm, "end": v(11.32, -146.64) * mm});
            skLineSegment(sketch, "E404", {"start": v(11.32, -146.64) * mm, "end": v(24.7, -149.38) * mm});
            skLineSegment(sketch, "E405", {"start": v(24.7, -149.38) * mm, "end": v(32.63, -151.76) * mm});
            skLineSegment(sketch, "E406", {"start": v(32.63, -151.76) * mm, "end": v(42.25, -153.99) * mm});
            skLineSegment(sketch, "E407", {"start": v(42.25, -153.99) * mm, "end": v(51.39, -156.1) * mm});
            skLineSegment(sketch, "E408", {"start": v(51.39, -156.1) * mm, "end": v(60.52, -155.82) * mm});
            skLineSegment(sketch, "E409", {"start": v(60.52, -155.82) * mm, "end": v(66.44, -155.16) * mm});
            skLineSegment(sketch, "E410", {"start": v(66.44, -155.16) * mm, "end": v(76.9, -153.18) * mm});
            skLineSegment(sketch, "E411", {"start": v(76.9, -153.18) * mm, "end": v(81.67, -151.08) * mm});
            skLineSegment(sketch, "E412", {"start": v(81.67, -151.08) * mm, "end": v(84.53, -149.32) * mm});
            skLineSegment(sketch, "E413", {"start": v(84.53, -149.32) * mm, "end": v(86.3, -148.25) * mm});
            skLineSegment(sketch, "E414", {"start": v(86.3, -148.25) * mm, "end": v(89.64, -148.58) * mm});
            skLineSegment(sketch, "E415", {"start": v(89.64, -148.58) * mm, "end": v(94.87, -150.34) * mm});
            skLineSegment(sketch, "E416", {"start": v(94.87, -150.34) * mm, "end": v(96.68, -150.95) * mm});
            skLineSegment(sketch, "E417", {"start": v(96.68, -150.95) * mm, "end": v(98.4, -151.53) * mm});
            skLineSegment(sketch, "E418", {"start": v(98.4, -151.53) * mm, "end": v(100.69, -150.96) * mm});
            skLineSegment(sketch, "E419", {"start": v(100.69, -150.96) * mm, "end": v(102.52, -149.55) * mm});
            skLineSegment(sketch, "E420", {"start": v(102.52, -149.55) * mm, "end": v(104.9, -146.9) * mm});
            skLineSegment(sketch, "E421", {"start": v(104.9, -146.9) * mm, "end": v(107.22, -143.51) * mm});
            skLineSegment(sketch, "E422", {"start": v(107.22, -143.51) * mm, "end": v(110.2, -138.16) * mm});
            skLineSegment(sketch, "E423", {"start": v(110.2, -138.16) * mm, "end": v(112.3, -134.36) * mm});
            skLineSegment(sketch, "E424", {"start": v(112.3, -134.36) * mm, "end": v(114.4, -127.06) * mm});
            skLineSegment(sketch, "E425", {"start": v(114.4, -127.06) * mm, "end": v(116.36, -117.54) * mm});
            skLineSegment(sketch, "E426", {"start": v(116.36, -117.54) * mm, "end": v(117.03, -114.36) * mm});
            skLineSegment(sketch, "E427", {"start": v(117.03, -114.36) * mm, "end": v(117.4, -108.27) * mm});
            skLineSegment(sketch, "E428", {"start": v(117.4, -108.27) * mm, "end": v(117.28, -102.88) * mm});
            skLineSegment(sketch, "E429", {"start": v(117.28, -102.88) * mm, "end": v(117.62, -96.41) * mm});
            skLineSegment(sketch, "E430", {"start": v(117.62, -96.41) * mm, "end": v(117.2, -90.99) * mm});
            skLineSegment(sketch, "E431", {"start": v(117.2, -90.99) * mm, "end": v(116.32, -83.37) * mm});
            skLineSegment(sketch, "E432", {"start": v(116.32, -83.37) * mm, "end": v(115, -78.83) * mm});
            skLineSegment(sketch, "E433", {"start": v(115, -78.83) * mm, "end": v(112.9, -73.83) * mm});
            skLineSegment(sketch, "E434", {"start": v(112.9, -73.83) * mm, "end": v(111.28, -70.01) * mm});
            skLineSegment(sketch, "E435", {"start": v(111.28, -70.01) * mm, "end": v(108.36, -66.85) * mm});
            skLineSegment(sketch, "E436", {"start": v(108.36, -66.85) * mm, "end": v(104.26, -62.42) * mm});
            skLineSegment(sketch, "E437", {"start": v(104.26, -62.42) * mm, "end": v(102.27, -60.26) * mm});
            skLineSegment(sketch, "E438", {"start": v(102.27, -60.26) * mm, "end": v(102.4, -57.28) * mm});
            skLineSegment(sketch, "E439", {"start": v(102.4, -57.28) * mm, "end": v(103.3, -49.54) * mm});
            skLineSegment(sketch, "E440", {"start": v(103.3, -49.54) * mm, "end": v(104.15, -42.4) * mm});
            skLineSegment(sketch, "E441", {"start": v(104.15, -42.4) * mm, "end": v(104.64, -38.32) * mm});
            skLineSegment(sketch, "E442", {"start": v(104.64, -38.32) * mm, "end": v(105.25, -37.8) * mm});
            skLineSegment(sketch, "E443", {"start": v(105.25, -37.8) * mm, "end": v(105.42, -34.63) * mm});
            skLineSegment(sketch, "E444", {"start": v(105.42, -34.63) * mm, "end": v(106.1, -29.53) * mm});
            skLineSegment(sketch, "E445", {"start": v(106.1, -29.53) * mm, "end": v(107.43, -23.21) * mm});
            skLineSegment(sketch, "E446", {"start": v(107.43, -23.21) * mm, "end": v(107.4, -21.23) * mm});
            skLineSegment(sketch, "E447", {"start": v(107.4, -21.23) * mm, "end": v(105.38, -18.7) * mm});
            skLineSegment(sketch, "E448", {"start": v(105.38, -18.7) * mm, "end": v(104.58, -17.06) * mm});
            skLineSegment(sketch, "E449", {"start": v(104.58, -17.06) * mm, "end": v(104.44, -15.92) * mm});
            skLineSegment(sketch, "E450", {"start": v(104.44, -15.92) * mm, "end": v(105.36, -12.25) * mm});
            skLineSegment(sketch, "E451", {"start": v(105.36, -12.25) * mm, "end": v(106.24, -8.71) * mm});
            skLineSegment(sketch, "E452", {"start": v(106.24, -8.71) * mm, "end": v(104.77, -5.92) * mm});
            skLineSegment(sketch, "E453", {"start": v(104.77, -5.92) * mm, "end": v(100.68, -5.04) * mm});
            skLineSegment(sketch, "E454", {"start": v(100.68, -5.04) * mm, "end": v(91.72, -7.01) * mm});
            skLineSegment(sketch, "E455", {"start": v(91.72, -7.01) * mm, "end": v(92.55, -9.67) * mm});
            skLineSegment(sketch, "E456", {"start": v(92.55, -9.67) * mm, "end": v(93.73, -11.8) * mm});
            skLineSegment(sketch, "E457", {"start": v(93.73, -11.8) * mm, "end": v(95.65, -15.26) * mm});
            skLineSegment(sketch, "E458", {"start": v(95.65, -15.26) * mm, "end": v(96.02, -16.87) * mm});
            skLineSegment(sketch, "E459", {"start": v(96.02, -16.87) * mm, "end": v(96.63, -19.57) * mm});
            skLineSegment(sketch, "E460", {"start": v(96.63, -19.57) * mm, "end": v(96.42, -24.03) * mm});
            skLineSegment(sketch, "E461", {"start": v(96.42, -24.03) * mm, "end": v(96.93, -25.97) * mm});
            skLineSegment(sketch, "E462", {"start": v(96.93, -25.97) * mm, "end": v(97.08, -29.58) * mm});
            skLineSegment(sketch, "E463", {"start": v(97.08, -29.58) * mm, "end": v(97.18, -32) * mm});
            skLineSegment(sketch, "E464", {"start": v(97.18, -32) * mm, "end": v(95, -40.81) * mm});
            skLineSegment(sketch, "E465", {"start": v(95, -40.81) * mm, "end": v(92.81, -49.67) * mm});
            skLineSegment(sketch, "E466", {"start": v(92.81, -49.67) * mm, "end": v(90.21, -54.76) * mm});
            skLineSegment(sketch, "E467", {"start": v(90.21, -54.76) * mm, "end": v(79.07, -54.3) * mm});
            skLineSegment(sketch, "E468", {"start": v(79.07, -54.3) * mm, "end": v(73.52, -54.5) * mm});
            skLineSegment(sketch, "E469", {"start": v(73.52, -54.5) * mm, "end": v(73.1, -50.93) * mm});
            skLineSegment(sketch, "E470", {"start": v(73.1, -50.93) * mm, "end": v(72.67, -47.4) * mm});
            skLineSegment(sketch, "E471", {"start": v(72.67, -47.4) * mm, "end": v(71.02, -44.05) * mm});
            skLineSegment(sketch, "E472", {"start": v(71.02, -44.05) * mm, "end": v(68.38, -38.66) * mm});
            skLineSegment(sketch, "E473", {"start": v(68.38, -38.66) * mm, "end": v(65.2, -32.17) * mm});
            skLineSegment(sketch, "E474", {"start": v(65.2, -32.17) * mm, "end": v(62.67, -23.64) * mm});
            skLineSegment(sketch, "E475", {"start": v(62.67, -23.64) * mm, "end": v(59.87, -16.25) * mm});
            skLineSegment(sketch, "E476", {"start": v(59.87, -16.25) * mm, "end": v(58.71, -15.08) * mm});
            skLineSegment(sketch, "E477", {"start": v(58.71, -15.08) * mm, "end": v(57.65, -14.74) * mm});
            skLineSegment(sketch, "E478", {"start": v(57.65, -14.74) * mm, "end": v(55.14, -14.65) * mm});
            skLineSegment(sketch, "E479", {"start": v(55.14, -14.65) * mm, "end": v(53.74, -13.72) * mm});
            skLineSegment(sketch, "E480", {"start": v(53.74, -13.72) * mm, "end": v(53.04, -12.62) * mm});
            skLineSegment(sketch, "E481", {"start": v(53.04, -12.62) * mm, "end": v(53.2, -10.57) * mm});
            skLineSegment(sketch, "E482", {"start": v(53.2, -10.57) * mm, "end": v(54.25, -7.05) * mm});
            skLineSegment(sketch, "E483", {"start": v(54.25, -7.05) * mm, "end": v(53.84, -5.66) * mm});
            skLineSegment(sketch, "E484", {"start": v(53.84, -5.66) * mm, "end": v(53.31, -3.9) * mm});
            skLineSegment(sketch, "E485", {"start": v(53.31, -3.9) * mm, "end": v(51.26, -3.61) * mm});
            skLineSegment(sketch, "E486", {"start": v(51.26, -3.61) * mm, "end": v(47.88, -3.13) * mm});
            skLineSegment(sketch, "E487", {"start": v(47.88, -3.13) * mm, "end": v(41.94, -2.72) * mm});
            skLineSegment(sketch, "E488", {"start": v(41.94, -2.72) * mm, "end": v(38.04, -3.7) * mm});
            skLineSegment(sketch, "E489", {"start": v(38.04, -3.7) * mm, "end": v(38.8, -6.86) * mm});
            skLineSegment(sketch, "E490", {"start": v(38.8, -6.86) * mm, "end": v(39.35, -9.2) * mm});
            skLineSegment(sketch, "E491", {"start": v(39.35, -9.2) * mm, "end": v(40.01, -12) * mm});
            skLineSegment(sketch, "E492", {"start": v(40.01, -12) * mm, "end": v(41.5, -13.83) * mm});
            skLineSegment(sketch, "E493", {"start": v(41.5, -13.83) * mm, "end": v(45.4, -17.36) * mm});
            skLineSegment(sketch, "E494", {"start": v(45.4, -17.36) * mm, "end": v(47.27, -18.5) * mm});
            skLineSegment(sketch, "E495", {"start": v(47.27, -18.5) * mm, "end": v(49.92, -22.03) * mm});
            skLineSegment(sketch, "E496", {"start": v(49.92, -22.03) * mm, "end": v(53.17, -27.4) * mm});
            skLineSegment(sketch, "E497", {"start": v(53.17, -27.4) * mm, "end": v(54.86, -32.04) * mm});
            skLineSegment(sketch, "E498", {"start": v(54.86, -32.04) * mm, "end": v(56.54, -36.65) * mm});
            skLineSegment(sketch, "E499", {"start": v(56.54, -36.65) * mm, "end": v(58.1, -42.48) * mm});
            skLineSegment(sketch, "E500", {"start": v(58.1, -42.48) * mm, "end": v(59.2, -46.6) * mm});
            skLineSegment(sketch, "E501", {"start": v(59.2, -46.6) * mm, "end": v(58.75, -53.56) * mm});
            skLineSegment(sketch, "E502", {"start": v(58.75, -53.56) * mm, "end": v(58.93, -57.95) * mm});
            skLineSegment(sketch, "E503", {"start": v(58.93, -57.95) * mm, "end": v(59.06, -61.25) * mm});
            skLineSegment(sketch, "E504", {"start": v(59.06, -61.25) * mm, "end": v(59.18, -64.28) * mm});
            skLineSegment(sketch, "E505", {"start": v(59.18, -64.28) * mm, "end": v(57.78, -68.02) * mm});
            skLineSegment(sketch, "E506", {"start": v(57.78, -68.02) * mm, "end": v(56.56, -71.28) * mm});
            skLineSegment(sketch, "E507", {"start": v(56.56, -71.28) * mm, "end": v(53.25, -79.8) * mm});
            skLineSegment(sketch, "E508", {"start": v(53.25, -79.8) * mm, "end": v(52.09, -84.29) * mm});
            skLineSegment(sketch, "E509", {"start": v(52.09, -84.29) * mm, "end": v(50.56, -88.05) * mm});
            skLineSegment(sketch, "E510", {"start": v(50.56, -88.05) * mm, "end": v(50.11, -92.26) * mm});
            skLineSegment(sketch, "E511", {"start": v(50.11, -92.26) * mm, "end": v(49.12, -93.93) * mm});
            skLineSegment(sketch, "E512", {"start": v(49.12, -93.93) * mm, "end": v(44.32, -91) * mm});
            skLineSegment(sketch, "E513", {"start": v(44.32, -91) * mm, "end": v(39.42, -87.08) * mm});
            skLineSegment(sketch, "E514", {"start": v(39.42, -87.08) * mm, "end": v(33.24, -83.21) * mm});
            skLineSegment(sketch, "E515", {"start": v(33.24, -83.21) * mm, "end": v(25.74, -79.62) * mm});
            skLineSegment(sketch, "E516", {"start": v(25.74, -79.62) * mm, "end": v(19.84, -77.93) * mm});
            skLineSegment(sketch, "E517", {"start": v(19.84, -77.93) * mm, "end": v(9.37, -76.37) * mm});
            skLineSegment(sketch, "E518", {"start": v(9.37, -76.37) * mm, "end": v(4.73, -76.37) * mm});
            skLineSegment(sketch, "E519", {"start": v(4.73, -76.37) * mm, "end": v(-4.99, -77.49) * mm});
            skLineSegment(sketch, "E520", {"start": v(-4.99, -77.49) * mm, "end": v(-14.97, -80.36) * mm});
            skLineSegment(sketch, "E521", {"start": v(-14.97, -80.36) * mm, "end": v(-18.72, -80.96) * mm});
            skLineSegment(sketch, "E522", {"start": v(-18.72, -80.96) * mm, "end": v(-19.66, -81.11) * mm});
            skLineSegment(sketch, "E523", {"start": v(-19.66, -81.11) * mm, "end": v(-19.68, -75.04) * mm});
            skLineSegment(sketch, "E524", {"start": v(-19.68, -75.04) * mm, "end": v(-18.33, -66.85) * mm});
            skLineSegment(sketch, "E525", {"start": v(-18.33, -66.85) * mm, "end": v(-16.06, -59.35) * mm});
            skLineSegment(sketch, "E526", {"start": v(-16.06, -59.35) * mm, "end": v(-15.2, -54.44) * mm});
            skLineSegment(sketch, "E527", {"start": v(-15.2, -54.44) * mm, "end": v(-14.93, -52.93) * mm});
            skLineSegment(sketch, "E528", {"start": v(-14.93, -52.93) * mm, "end": v(-14.97, -49.46) * mm});
            skLineSegment(sketch, "E529", {"start": v(-14.97, -49.46) * mm, "end": v(-14.6, -45.87) * mm});
            skLineSegment(sketch, "E530", {"start": v(-14.6, -45.87) * mm, "end": v(-13.42, -39.78) * mm});
            skLineSegment(sketch, "E531", {"start": v(-13.42, -39.78) * mm, "end": v(-11.85, -35.53) * mm});
            skLineSegment(sketch, "E532", {"start": v(-11.85, -35.53) * mm, "end": v(-8.92, -27.59) * mm});
            skLineSegment(sketch, "E533", {"start": v(-8.92, -27.59) * mm, "end": v(-6.5, -21.06) * mm});
            skLineSegment(sketch, "E534", {"start": v(-6.5, -21.06) * mm, "end": v(-5.77, -19.05) * mm});
            skLineSegment(sketch, "E535", {"start": v(-5.77, -19.05) * mm, "end": v(-5.93, -17.3) * mm});
            skLineSegment(sketch, "E536", {"start": v(-5.93, -17.3) * mm, "end": v(-7.94, -15.85) * mm});
            skLineSegment(sketch, "E537", {"start": v(-7.94, -15.85) * mm, "end": v(-10.62, -14.45) * mm});
            skLineSegment(sketch, "E538", {"start": v(-10.62, -14.45) * mm, "end": v(-11.17, -12.98) * mm});
            skLineSegment(sketch, "E539", {"start": v(-11.17, -12.98) * mm, "end": v(-10.86, -11.5) * mm});
            skLineSegment(sketch, "E540", {"start": v(-10.86, -11.5) * mm, "end": v(-9.54, -9.82) * mm});
            skLineSegment(sketch, "E541", {"start": v(-9.54, -9.82) * mm, "end": v(-8.36, -8.34) * mm});
            skLineSegment(sketch, "E542", {"start": v(-8.36, -8.34) * mm, "end": v(-7.82, -5.86) * mm});
            skLineSegment(sketch, "E543", {"start": v(-7.82, -5.86) * mm, "end": v(-8.05, -2.37) * mm});
            skLineSegment(sketch, "E544", {"start": v(-8.05, -2.37) * mm, "end": v(-10.77, -1.38) * mm});
            skLineSegment(sketch, "E545", {"start": v(-10.77, -1.38) * mm, "end": v(-15.9, -0.36) * mm});
            skLineSegment(sketch, "E546", {"start": v(-15.9, -0.36) * mm, "end": v(-19.71, -0.44) * mm});
            skLineSegment(sketch, "E547", {"start": v(-19.71, -0.44) * mm, "end": v(-23.88, -1.6) * mm});
            skLineSegment(sketch, "E548", {"start": v(-23.88, -1.6) * mm, "end": v(-23.16, -5.34) * mm});
            skLineSegment(sketch, "E549", {"start": v(-23.16, -5.34) * mm, "end": v(-20.88, -9.55) * mm});
            skLineSegment(sketch, "E550", {"start": v(-20.88, -9.55) * mm, "end": v(-19.35, -12.37) * mm});
            skLineSegment(sketch, "E551", {"start": v(-19.35, -12.37) * mm, "end": v(-18.34, -15.22) * mm});
            skLineSegment(sketch, "E552", {"start": v(-18.34, -15.22) * mm, "end": v(-16.25, -19.93) * mm});
            skLineSegment(sketch, "E553", {"start": v(-16.25, -19.93) * mm, "end": v(-16.66, -24.5) * mm});
            skLineSegment(sketch, "E554", {"start": v(-16.66, -24.5) * mm, "end": v(-18.12, -28.63) * mm});
            skLineSegment(sketch, "E555", {"start": v(-18.12, -28.63) * mm, "end": v(-21.4, -35.83) * mm});
            skLineSegment(sketch, "E556", {"start": v(-21.4, -35.83) * mm, "end": v(-22.92, -38.18) * mm});
            skLineSegment(sketch, "E557", {"start": v(-22.92, -38.18) * mm, "end": v(-24.52, -41.43) * mm});
            skLineSegment(sketch, "E558", {"start": v(-24.52, -41.43) * mm, "end": v(-26.3, -45.03) * mm});
            skLineSegment(sketch, "E559", {"start": v(-26.3, -45.03) * mm, "end": v(-28.06, -52.7) * mm});
            skLineSegment(sketch, "E560", {"start": v(-28.06, -52.7) * mm, "end": v(-29.83, -58.38) * mm});
            skLineSegment(sketch, "E561", {"start": v(-29.83, -58.38) * mm, "end": v(-31.75, -62.86) * mm});
            skLineSegment(sketch, "E562", {"start": v(-31.75, -62.86) * mm, "end": v(-36.9, -70.97) * mm});
            skLineSegment(sketch, "E563", {"start": v(-36.9, -70.97) * mm, "end": v(-40.15, -60.28) * mm});
            skLineSegment(sketch, "E564", {"start": v(-40.15, -60.28) * mm, "end": v(-42.8, -51.57) * mm});
            skLineSegment(sketch, "E565", {"start": v(-42.8, -51.57) * mm, "end": v(-43.4, -49.58) * mm});
            skLineSegment(sketch, "E566", {"start": v(-43.4, -49.58) * mm, "end": v(-44.58, -47.68) * mm});
            skLineSegment(sketch, "E567", {"start": v(-44.58, -47.68) * mm, "end": v(-46.4, -44.7) * mm});
            skLineSegment(sketch, "E568", {"start": v(-46.4, -44.7) * mm, "end": v(-46.78, -43) * mm});
            skLineSegment(sketch, "E569", {"start": v(-46.78, -43) * mm, "end": v(-47.84, -35.67) * mm});
            skLineSegment(sketch, "E570", {"start": v(-47.84, -35.67) * mm, "end": v(-48.97, -27.88) * mm});
            skLineSegment(sketch, "E571", {"start": v(-48.97, -27.88) * mm, "end": v(-50.09, -20.12) * mm});
            skLineSegment(sketch, "E572", {"start": v(-50.09, -20.12) * mm, "end": v(-50.39, -18.03) * mm});
            skLineSegment(sketch, "E573", {"start": v(-50.39, -18.03) * mm, "end": v(-51.54, -16.72) * mm});
            skLineSegment(sketch, "E574", {"start": v(-51.54, -16.72) * mm, "end": v(-54.37, -15.95) * mm});
            skLineSegment(sketch, "E575", {"start": v(-54.37, -15.95) * mm, "end": v(-56.96, -15.66) * mm});
            skLineSegment(sketch, "E576", {"start": v(-56.96, -15.66) * mm, "end": v(-57.93, -14.8) * mm});
            skLineSegment(sketch, "E577", {"start": v(-57.93, -14.8) * mm, "end": v(-58.06, -12.59) * mm});
            skLineSegment(sketch, "E578", {"start": v(-58.06, -12.59) * mm, "end": v(-56.6, -8.03) * mm});
            skLineSegment(sketch, "E579", {"start": v(-56.6, -8.03) * mm, "end": v(-58.29, -4.76) * mm});
            skLineSegment(sketch, "E580", {"start": v(-58.29, -4.76) * mm, "end": v(-59.1, -4.45) * mm});
            skLineSegment(sketch, "E581", {"start": v(-59.1, -4.45) * mm, "end": v(-63.73, -4.25) * mm});
            skLineSegment(sketch, "E582", {"start": v(-63.73, -4.25) * mm, "end": v(-68.56, -4.51) * mm});
            skLineSegment(sketch, "E583", {"start": v(-68.56, -4.51) * mm, "end": v(-70.55, -5.1) * mm});
            skLineSegment(sketch, "E584", {"start": v(-70.55, -5.1) * mm, "end": v(-71.68, -6.13) * mm});
            skLineSegment(sketch, "E585", {"start": v(-71.68, -6.13) * mm, "end": v(-71.1, -9.16) * mm});
            skLineSegment(sketch, "E586", {"start": v(-71.1, -9.16) * mm, "end": v(-69.7, -11.64) * mm});
            skLineSegment(sketch, "E587", {"start": v(-69.7, -11.64) * mm, "end": v(-67.26, -14.8) * mm});
            skLineSegment(sketch, "E588", {"start": v(-67.26, -14.8) * mm, "end": v(-64.88, -16.36) * mm});
            skLineSegment(sketch, "E589", {"start": v(-64.88, -16.36) * mm, "end": v(-62.63, -17.83) * mm});
            skLineSegment(sketch, "E590", {"start": v(-62.63, -17.83) * mm, "end": v(-60.88, -20.47) * mm});
            skLineSegment(sketch, "E591", {"start": v(-60.88, -20.47) * mm, "end": v(-60.04, -23.79) * mm});
            skLineSegment(sketch, "E592", {"start": v(-60.04, -23.79) * mm, "end": v(-59.49, -24.28) * mm});
            skLineSegment(sketch, "E593", {"start": v(-59.49, -24.28) * mm, "end": v(-58.98, -26.75) * mm});
            skLineSegment(sketch, "E594", {"start": v(-58.98, -26.75) * mm, "end": v(-57.92, -31.98) * mm});
            skLineSegment(sketch, "E595", {"start": v(-57.92, -31.98) * mm, "end": v(-57.02, -42.83) * mm});
            skLineSegment(sketch, "E596", {"start": v(-57.02, -42.83) * mm, "end": v(-56.55, -48.57) * mm});
            skLineSegment(sketch, "E597", {"start": v(-56.55, -48.57) * mm, "end": v(-56.03, -53.06) * mm});
            skLineSegment(sketch, "E598", {"start": v(-56.03, -53.06) * mm, "end": v(-55.19, -55.62) * mm});
            skLineSegment(sketch, "E599", {"start": v(-55.19, -55.62) * mm, "end": v(-53.64, -58.85) * mm});
            skLineSegment(sketch, "E600", {"start": v(-53.64, -58.85) * mm, "end": v(-53.14, -60.88) * mm});
            skLineSegment(sketch, "E601", {"start": v(-53.14, -60.88) * mm, "end": v(-52.71, -68.3) * mm});
            skLineSegment(sketch, "E602", {"start": v(-52.71, -68.3) * mm, "end": v(-53.03, -75.04) * mm});
            skLineSegment(sketch, "E603", {"start": v(-53.03, -75.04) * mm, "end": v(-53.2, -78.41) * mm});
            skLineSegment(sketch, "E604", {"start": v(-53.2, -78.41) * mm, "end": v(-54.68, -84.27) * mm});
            skLineSegment(sketch, "E605", {"start": v(-54.68, -84.27) * mm, "end": v(-55.88, -84.67) * mm});
            skLineSegment(sketch, "E606", {"start": v(-55.88, -84.67) * mm, "end": v(-58.82, -86.81) * mm});
            skLineSegment(sketch, "E607", {"start": v(-58.82, -86.81) * mm, "end": v(-60.13, -87.77) * mm});
            skLineSegment(sketch, "E608", {"start": v(-60.13, -87.77) * mm, "end": v(-63.38, -85.99) * mm});
            skLineSegment(sketch, "E609", {"start": v(-63.38, -85.99) * mm, "end": v(-67.1, -83.34) * mm});
            skLineSegment(sketch, "E610", {"start": v(-67.1, -83.34) * mm, "end": v(-69.73, -80.77) * mm});
            skLineSegment(sketch, "E611", {"start": v(-69.73, -80.77) * mm, "end": v(-72.8, -76.82) * mm});
            skLineSegment(sketch, "E612", {"start": v(-72.8, -76.82) * mm, "end": v(-75.53, -72.5) * mm});
            skLineSegment(sketch, "E613", {"start": v(-75.53, -72.5) * mm, "end": v(-77.45, -68.7) * mm});
            skLineSegment(sketch, "E614", {"start": v(-77.45, -68.7) * mm, "end": v(-79.89, -64.93) * mm});
            skLineSegment(sketch, "E615", {"start": v(-79.89, -64.93) * mm, "end": v(-82.24, -59.75) * mm});
            skLineSegment(sketch, "E616", {"start": v(-82.24, -59.75) * mm, "end": v(-83.46, -57.05) * mm});
            skLineSegment(sketch, "E617", {"start": v(-83.46, -57.05) * mm, "end": v(-84.38, -52.2) * mm});
            skLineSegment(sketch, "E618", {"start": v(-84.38, -52.2) * mm, "end": v(-85.23, -47.75) * mm});
            skLineSegment(sketch, "E619", {"start": v(-85.23, -47.75) * mm, "end": v(-83.98, -44.5) * mm});
            skLineSegment(sketch, "E620", {"start": v(-83.98, -44.5) * mm, "end": v(-83.46, -43.13) * mm});
            skLineSegment(sketch, "E621", {"start": v(-83.46, -43.13) * mm, "end": v(-83.73, -41.84) * mm});
            skLineSegment(sketch, "E622", {"start": v(-83.73, -41.84) * mm, "end": v(-83.41, -39.7) * mm});
            skLineSegment(sketch, "E623", {"start": v(-83.41, -39.7) * mm, "end": v(-83.76, -36.48) * mm});
            skLineSegment(sketch, "E624", {"start": v(-83.76, -36.48) * mm, "end": v(-85.08, -32.91) * mm});
            skLineSegment(sketch, "E625", {"start": v(-85.08, -32.91) * mm, "end": v(-86.38, -31.06) * mm});
            skLineSegment(sketch, "E626", {"start": v(-86.38, -31.06) * mm, "end": v(-88.06, -28.65) * mm});
            skLineSegment(sketch, "E627", {"start": v(-88.06, -28.65) * mm, "end": v(-90.46, -27.44) * mm});
            skLineSegment(sketch, "E628", {"start": v(-90.46, -27.44) * mm, "end": v(-92.94, -23.52) * mm});
            skLineSegment(sketch, "E629", {"start": v(-92.94, -23.52) * mm, "end": v(-98.53, -16.05) * mm});
            skLineSegment(sketch, "E630", {"start": v(-98.53, -16.05) * mm, "end": v(-100.37, -13.6) * mm});
            skLineSegment(sketch, "E631", {"start": v(-100.37, -13.6) * mm, "end": v(-99.76, -11.74) * mm});
            skLineSegment(sketch, "E632", {"start": v(-99.76, -11.74) * mm, "end": v(-99.52, -9.15) * mm});
            skLineSegment(sketch, "E633", {"start": v(-99.52, -9.15) * mm, "end": v(-100.33, -4.42) * mm});
            skSolve(sketch);
        }
        {
            var Q0;
            Q0=makeQuery(id+"F0.imprint","IMPRINT",FACE,{"disambiguationData":[TD([[makeQuery(id+"F0.imprint","IMPRINT",EDGE,{"derivedFrom":sQuery(id+"F0.wireOp",EDGE,"E317")}),1.0]])]});
            var Q1;
            Q1=makeQuery(id+"F0.imprint","IMPRINT",FACE,{"disambiguationData":[TD([[makeQuery(id+"F0.imprint","IMPRINT",EDGE,{"derivedFrom":sQuery(id+"F0.wireOp",EDGE,"E0")}),-1.0]])]});
            extrude(context, id + "F1", {"entities" : qUnion([Q0, Q1]), "depth" : 7.94 * mm, "offsetDistance" : 25.4 * mm});
        }
    });
